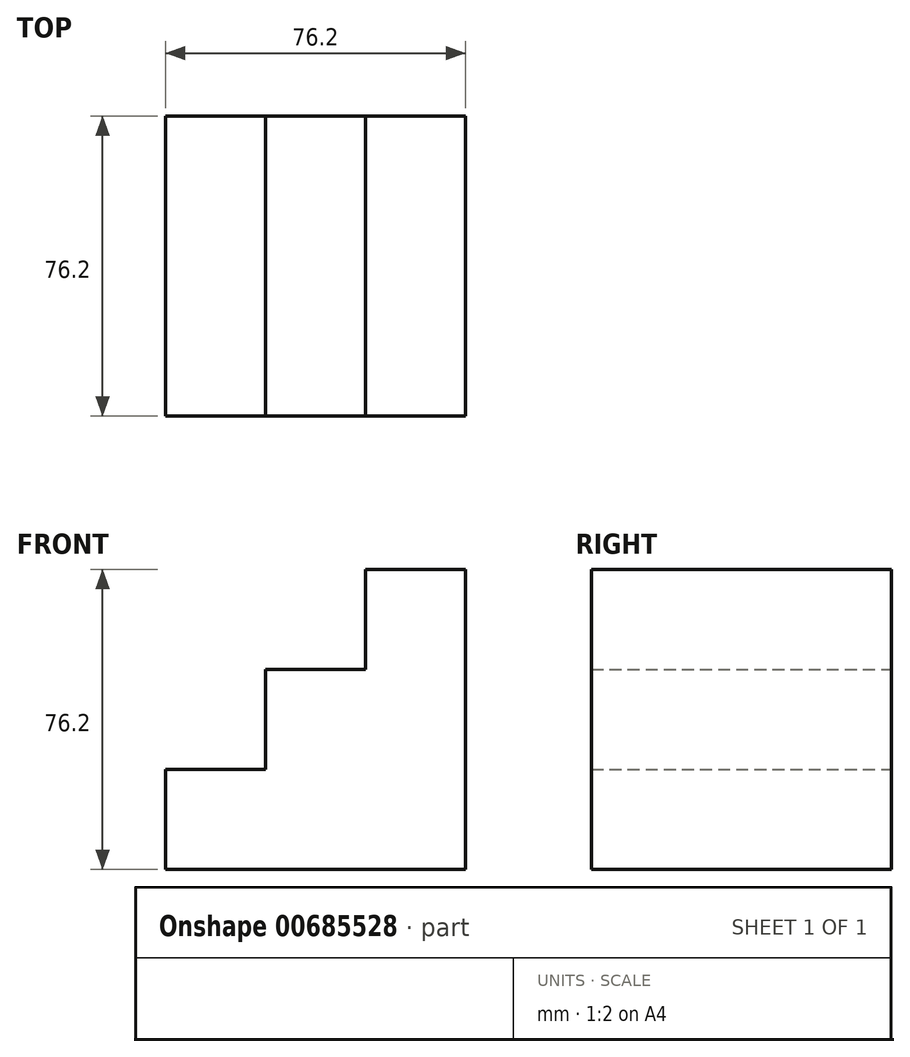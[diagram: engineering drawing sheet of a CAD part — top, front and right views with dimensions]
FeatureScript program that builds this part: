
annotation { "Feature Type Name" : "Feature", "Feature Type Description" : "" }
export const myFeature = defineFeature(function(context is Context, id is Id, definition is map)
    precondition{}
    {
        {
            var Q0;
            Q0=qCreatedBy(makeId("Front.planeOp"),FACE);
            var sketch = newSketch(context, id + "F0", { "sketchPlane" : qUnion([Q0])});
            skLineSegment(sketch, "E0", {"start": v(0, 0) * mm, "end": v(76.2, 0) * mm});
            skLineSegment(sketch, "E1", {"start": v(76.2, 0) * mm, "end": v(76.2, 76.2) * mm});
            skLineSegment(sketch, "E2", {"start": v(76.2, 76.2) * mm, "end": v(50.8, 76.2) * mm});
            skLineSegment(sketch, "E3", {"start": v(50.8, 76.2) * mm, "end": v(50.8, 50.8) * mm});
            skLineSegment(sketch, "E4", {"start": v(50.8, 50.8) * mm, "end": v(25.4, 50.8) * mm});
            skLineSegment(sketch, "E5", {"start": v(25.4, 50.8) * mm, "end": v(25.4, 25.4) * mm});
            skLineSegment(sketch, "E6", {"start": v(25.4, 25.4) * mm, "end": v(0, 25.4) * mm});
            skLineSegment(sketch, "E7", {"start": v(0, 25.4) * mm, "end": v(0, 0) * mm});
            skSolve(sketch);
        }
        {
            var Q0;
            Q0=makeQuery(id+"F0.imprint","IMPRINT",FACE,{"disambiguationData":[TD([[makeQuery(id+"F0.imprint","IMPRINT",EDGE,{"derivedFrom":sQuery(id+"F0.wireOp",EDGE,"E0")}),1.0]])]});
            extrude(context, id + "F1", {"entities" : qUnion([Q0]), "depth" : 76.2 * mm, "offsetDistance" : 25.4 * mm});
        }
    });
